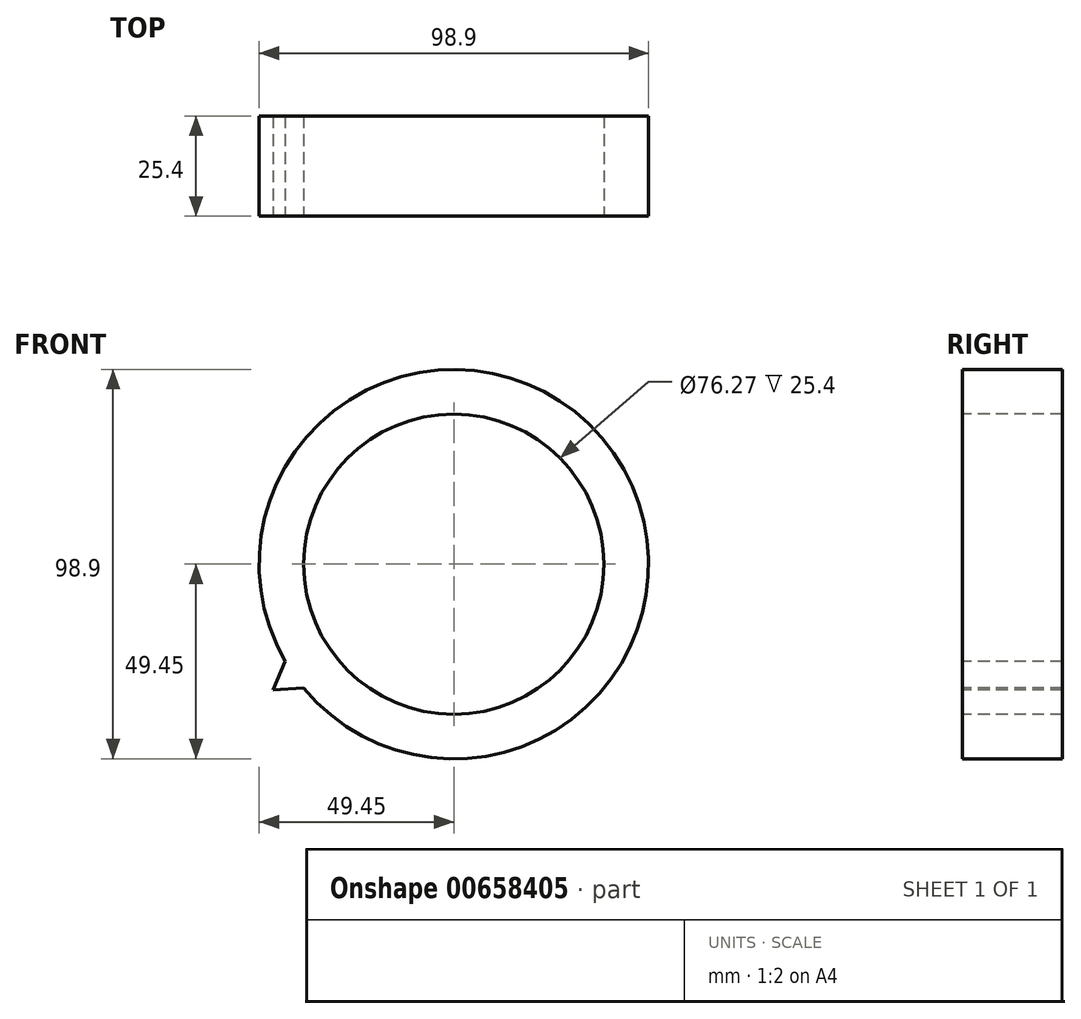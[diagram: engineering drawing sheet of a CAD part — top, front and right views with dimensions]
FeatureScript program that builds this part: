
annotation { "Feature Type Name" : "Feature", "Feature Type Description" : "" }
export const myFeature = defineFeature(function(context is Context, id is Id, definition is map)
    precondition{}
    {
        {
            var Q0;
            Q0=qCreatedBy(makeId("Front.planeOp"),FACE);
            var sketch = newSketch(context, id + "F0", { "sketchPlane" : qUnion([Q0])});
            skCircle(sketch, "E0", {"center": v(0, 0) * mm, "radius": 49.45 * mm});
            skSolve(sketch);
        }
        {
            var Q0;
            Q0=makeQuery(id+"F0.imprint","IMPRINT",FACE,{"disambiguationData":[TD([[makeQuery(id+"F0.imprint","IMPRINT",EDGE,{"derivedFrom":sQuery(id+"F0.wireOp",EDGE,"E0")}),1.0]])]});
            extrude(context, id + "F1", {"entities" : qUnion([Q0]), "depth" : 25.4 * mm, "offsetDistance" : 25.4 * mm});
        }
        {
            var Q0;
            Q0=makeQuery(id+"F1.opExtrude","CAP_FACE",FACE,{"disambiguationData":[OSD([sQuery(id+"F0.wireOp",EDGE,"E0")])],"isStart":false});
            var sketch = newSketch(context, id + "F2", { "sketchPlane" : qUnion([Q0])});
            skLineSegment(sketch, "E1", {"start": v(-42.85, -24.7) * mm, "end": v(-45.85, -31.98) * mm});
            skLineSegment(sketch, "E2", {"start": v(-45.85, -31.98) * mm, "end": v(-38.13, -31.5) * mm});
            skLineSegment(sketch, "E3", {"start": v(-38.13, -31.5) * mm, "end": v(-42.85, -24.7) * mm});
            skSolve(sketch);
        }
        {
            var Q0;
            {var subQ0=sQuery(id+"F2.wireOp",EDGE,"E1");Q0=makeQuery(id+"F2.imprint","IMPRINT",FACE,{"disambiguationData":[TD([[makeQuery(id+"F2.imprint","IMPRINT",EDGE,{"derivedFrom":subQ0}),1.0]])]});}
            extrude(context, id + "F3", {"entities" : qUnion([Q0]), "operationType" : NewBodyOperationType.ADD, "oppositeDirection" : true, "depth" : 25.4 * mm, "offsetDistance" : 25.4 * mm});
        }
        {
            var Q0;
            Q0=qCreatedBy(makeId("Right.planeOp"),FACE);
            var sketch = newSketch(context, id + "F4", { "sketchPlane" : qUnion([Q0])});
            skLineSegment(sketch, "E4.bottom", {"start": v(0, 0) * mm, "end": v(-46.77, 0) * mm});
            skLineSegment(sketch, "E4.top", {"start": v(0, 38.13) * mm, "end": v(-46.77, 38.13) * mm});
            skLineSegment(sketch, "E4.left", {"start": v(0, 0) * mm, "end": v(0, 38.13) * mm});
            skLineSegment(sketch, "E4.right", {"start": v(-46.77, 0) * mm, "end": v(-46.77, 38.13) * mm});
            skSolve(sketch);
        }
        {
            var Q0;
            Q0=makeQuery(id+"F4.imprint","IMPRINT",FACE,{"disambiguationData":[TD([[makeQuery(id+"F4.imprint","IMPRINT",EDGE,{"derivedFrom":sQuery(id+"F4.wireOp",EDGE,"E4.bottom")}),-1.0]])]});
            var Q1;
            Q1=sQuery(id+"F4.wireOp",EDGE,"E4.bottom");
            revolve(context, id + "F5", {"operationType" : NewBodyOperationType.REMOVE, "entities" : qUnion([Q0]), "axis" : qUnion([Q1]), "revolveType" : RevolveType.FULL, "oppositeDirection" : true});
        }
    });
